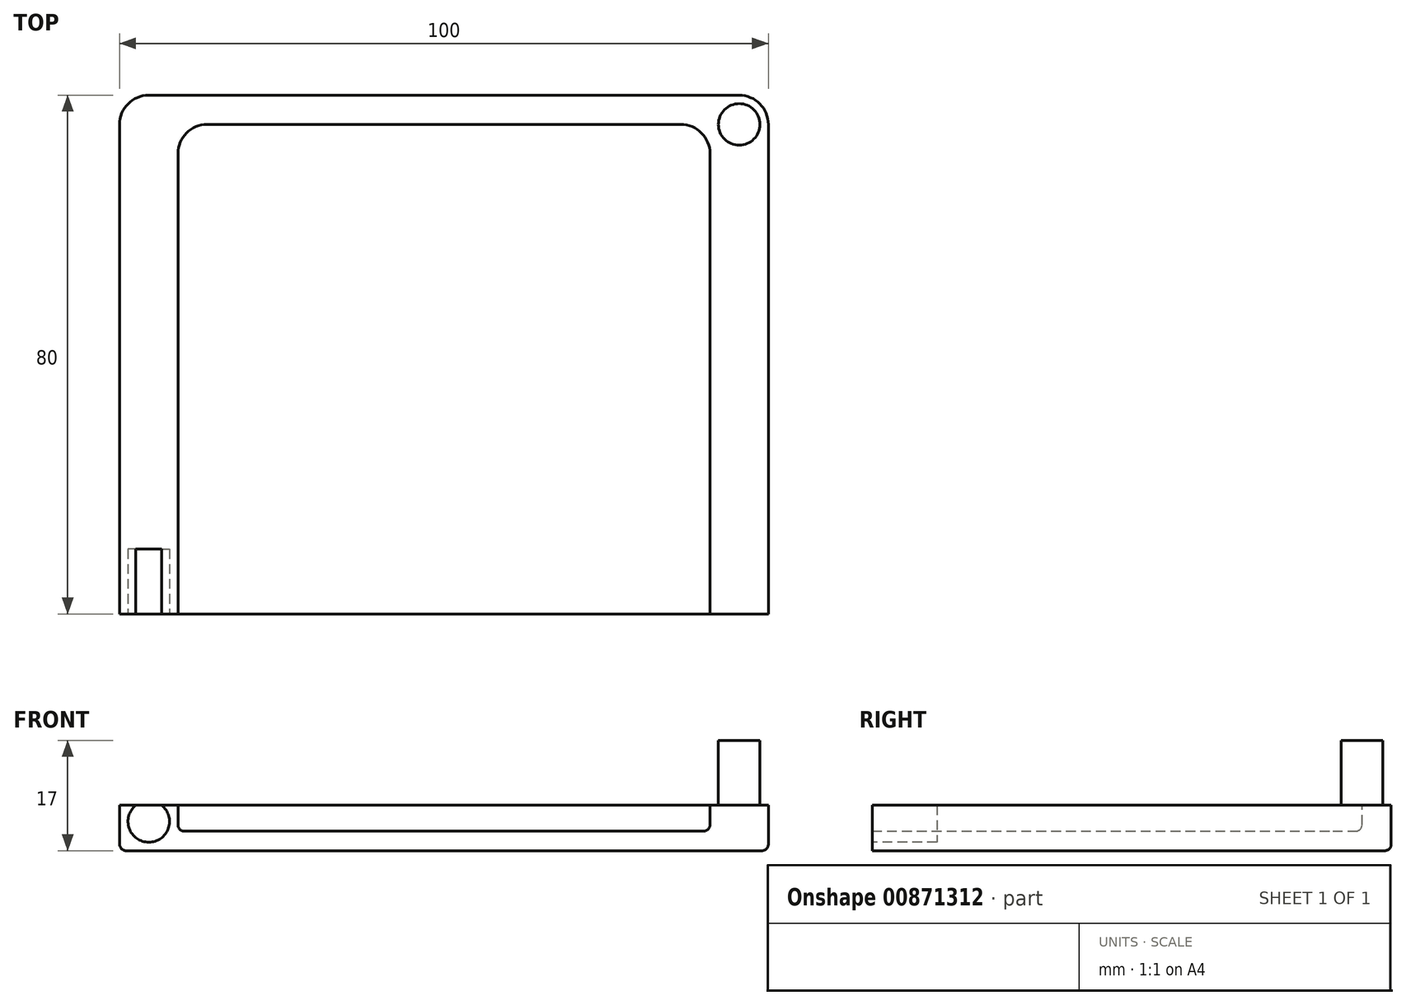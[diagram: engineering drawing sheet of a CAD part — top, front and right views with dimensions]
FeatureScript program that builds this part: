
annotation { "Feature Type Name" : "Feature", "Feature Type Description" : "" }
export const myFeature = defineFeature(function(context is Context, id is Id, definition is map)
    precondition{}
    {
        {
            var Q0;
            Q0=qCreatedBy(makeId("Top.planeOp"),FACE);
            var sketch = newSketch(context, id + "F0", { "sketchPlane" : qUnion([Q0])});
            skLineSegment(sketch, "E0.bottom", {"start": v(0, 0) * mm, "end": v(50, 0) * mm});
            skLineSegment(sketch, "E0.top", {"start": v(4.5, 80) * mm, "end": v(50, 80) * mm});
            skLineSegment(sketch, "E0.left", {"start": v(0, 0) * mm, "end": v(0, 75.5) * mm});
            skLineSegment(sketch, "E0.right", {"start": v(50, 0) * mm, "end": v(50, 80) * mm, "construction": true});
            skPoint(sketch, "E1.visualSharp", {"position": v(0, 80) * mm});
            skArc(sketch, "E1.filletArc", {"start": v(4.5, 80) * mm, "mid": v(1.32, 78.68) * mm, "end": v(0, 75.5) * mm});
            skArc(sketch, "E2.MirrorCS", {"start": v(95.5, 80) * mm, "mid": v(98.68, 78.68) * mm, "end": v(100, 75.5) * mm});
            skLineSegment(sketch, "E3.MirrorCS", {"start": v(100, 0) * mm, "end": v(50, 0) * mm});
            skPoint(sketch, "E4.MirrorP", {"position": v(100, 80) * mm});
            skLineSegment(sketch, "E5.MirrorCS", {"start": v(95.5, 80) * mm, "end": v(50, 80) * mm});
            skLineSegment(sketch, "E6.MirrorCS", {"start": v(100, 0) * mm, "end": v(100, 75.5) * mm});
            skSolve(sketch);
        }
        {
            var Q0;
            Q0=makeQuery(id+"F0.imprint","IMPRINT",FACE,{"disambiguationData":[TD([[makeQuery(id+"F0.imprint","IMPRINT",EDGE,{"derivedFrom":sQuery(id+"F0.wireOp",EDGE,"E0.bottom")}),1.0]])]});
            extrude(context, id + "F1", {"entities" : qUnion([Q0]), "depth" : 17 * mm, "offsetDistance" : 25 * mm});
        }
        {
            var Q0;
            Q0=qCreatedBy(makeId("Top.planeOp"),FACE);
            cPlane(context, id + "F2", {"entities" : qUnion([Q0]), "cplaneType" : CPlaneType.OFFSET, "offset" : 17 * mm, "width" : 150 * mm, "height" : 150 * mm});
        }
        {
            var Q0;
            Q0=qCreatedBy(id+"F2.planeOp",FACE);
            var sketch = newSketch(context, id + "F3", { "sketchPlane" : qUnion([Q0])});
            skLineSegment(sketch, "E7.bottom", {"start": v(0, 0) * mm, "end": v(50, 0) * mm});
            skLineSegment(sketch, "E7.top", {"start": v(4.5, 80) * mm, "end": v(50, 80) * mm});
            skLineSegment(sketch, "E7.left", {"start": v(0, 0) * mm, "end": v(0, 75.5) * mm});
            skLineSegment(sketch, "E7.right", {"start": v(50, 0) * mm, "end": v(50, 80) * mm, "construction": true});
            skPoint(sketch, "E8.visualSharp", {"position": v(0, 80) * mm});
            skArc(sketch, "E8.filletArc", {"start": v(4.5, 80) * mm, "mid": v(1.32, 78.68) * mm, "end": v(0, 75.5) * mm});
            skCircle(sketch, "E9", {"center": v(4.5, 75.5) * mm, "radius": 3.2 * mm});
            skLineSegment(sketch, "E10", {"start": v(9, 0) * mm, "end": v(9, 71) * mm});
            skLineSegment(sketch, "E11", {"start": v(13.5, 75.5) * mm, "end": v(50, 75.5) * mm});
            skPoint(sketch, "E12.visualSharp", {"position": v(9, 75.5) * mm});
            skArc(sketch, "E12.filletArc", {"start": v(13.5, 75.5) * mm, "mid": v(10.32, 74.18) * mm, "end": v(9, 71) * mm});
            skArc(sketch, "E13.MirrorCS", {"start": v(86.5, 75.5) * mm, "mid": v(89.68, 74.18) * mm, "end": v(91, 71) * mm});
            skArc(sketch, "E14.MirrorCS", {"start": v(95.5, 80) * mm, "mid": v(98.68, 78.68) * mm, "end": v(100, 75.5) * mm});
            skPoint(sketch, "E15.MirrorP", {"position": v(91, 75.5) * mm});
            skLineSegment(sketch, "E16.MirrorCS", {"start": v(91, 0) * mm, "end": v(91, 71) * mm});
            skLineSegment(sketch, "E17.MirrorCS", {"start": v(86.5, 75.5) * mm, "end": v(50, 75.5) * mm});
            skCircle(sketch, "E18.MirrorC", {"center": v(95.5, 75.5) * mm, "radius": 3.2 * mm});
            skLineSegment(sketch, "E19.MirrorCS", {"start": v(100, 0) * mm, "end": v(50, 0) * mm});
            skPoint(sketch, "E20.MirrorP", {"position": v(100, 80) * mm});
            skLineSegment(sketch, "E21.MirrorCS", {"start": v(95.5, 80) * mm, "end": v(50, 80) * mm});
            skLineSegment(sketch, "E22.MirrorCS", {"start": v(100, 0) * mm, "end": v(100, 75.5) * mm});
            skSolve(sketch);
        }
        {
            var Q0;
            Q0=qCreatedBy(makeId("Front.planeOp"),FACE);
            var sketch = newSketch(context, id + "F4", { "sketchPlane" : qUnion([Q0])});
            skLineSegment(sketch, "E23", {"start": v(50, 28.4) * mm, "end": v(50, -10.45) * mm, "construction": true});
            skCircle(sketch, "E24", {"center": v(4.5, 4.5) * mm, "radius": 3.2 * mm});
            skCircle(sketch, "E25.MirrorC", {"center": v(95.5, 4.5) * mm, "radius": 3.2 * mm});
            skSolve(sketch);
        }
        {
            var Q0;
            {var subQ0=sQuery(id+"F3.wireOp",EDGE,"E10");Q0=makeQuery(id+"F3.imprint","IMPRINT",FACE,{"disambiguationData":[TD([[makeQuery(id+"F3.imprint","IMPRINT",EDGE,{"derivedFrom":subQ0}),-1.0]])]});}
            extrude(context, id + "F5", {"entities" : qUnion([Q0]), "operationType" : NewBodyOperationType.REMOVE, "oppositeDirection" : true, "depth" : 14 * mm, "offsetDistance" : 25 * mm});
        }
        {
            var Q0;
            Q0=makeQuery(id+"F3.imprint","IMPRINT",FACE,{"disambiguationData":[TD([[makeQuery(id+"F3.imprint","IMPRINT",EDGE,{"derivedFrom":sQuery(id+"F3.wireOp",EDGE,"E9")}),1.0]])]});
            var Q1;
            Q1=makeQuery(id+"F3.imprint","IMPRINT",FACE,{"disambiguationData":[TD([[makeQuery(id+"F3.imprint","IMPRINT",EDGE,{"derivedFrom":sQuery(id+"F3.wireOp",EDGE,"E18.MirrorC")}),-1.0]])]});
            extrude(context, id + "F6", {"entities" : qUnion([Q0, Q1]), "operationType" : NewBodyOperationType.REMOVE, "oppositeDirection" : true, "depth" : 10 * mm, "offsetDistance" : 25 * mm});
        }
        {
            var Q0;
            Q0=makeQuery(id+"F4.imprint","IMPRINT",FACE,{"disambiguationData":[TD([[makeQuery(id+"F4.imprint","IMPRINT",EDGE,{"derivedFrom":sQuery(id+"F4.wireOp",EDGE,"E24")}),1.0]])]});
            var Q1;
            Q1=makeQuery(id+"F4.imprint","IMPRINT",FACE,{"disambiguationData":[TD([[makeQuery(id+"F4.imprint","IMPRINT",EDGE,{"derivedFrom":sQuery(id+"F4.wireOp",EDGE,"E25.MirrorC")}),-1.0]])]});
            extrude(context, id + "F7", {"entities" : qUnion([Q0, Q1]), "operationType" : NewBodyOperationType.REMOVE, "oppositeDirection" : true, "depth" : 10 * mm, "offsetDistance" : 25 * mm});
        }
        {
            var Q0;
            Q0=makeQuery(id+"F5.boolean.opBoolean","COPY",EDGE,{"derivedFrom":makeQuery(id+"F5.opExtrude","CAP_EDGE",EDGE,{"disambiguationData":[OSD([sQuery(id+"F3.wireOp",EDGE,"E11"),sQuery(id+"F3.wireOp",EDGE,"E17.MirrorCS")])],"isStart":false})});
            var Q1;
            Q1=makeQuery(id+"F1.opExtrude","CAP_EDGE",EDGE,{"disambiguationData":[OSD([sQuery(id+"F0.wireOp",EDGE,"E6.MirrorCS")])],"isStart":false});
            var Q2;
            Q2=makeQuery(id+"F1.opExtrude","CAP_EDGE",EDGE,{"disambiguationData":[OSD([sQuery(id+"F0.wireOp",EDGE,"E6.MirrorCS")])],"isStart":true});
            var Q3;
            Q3=makeQuery(id+"F7.boolean.opBoolean","COPY",EDGE,{"derivedFrom":makeQuery(id+"F7.opExtrude","CAP_EDGE",EDGE,{"disambiguationData":[OSD([sQuery(id+"F4.wireOp",EDGE,"E24")])],"isStart":true})});
            var Q4;
            Q4=makeQuery(id+"F7.boolean.opBoolean","COPY",EDGE,{"derivedFrom":makeQuery(id+"F7.opExtrude","CAP_EDGE",EDGE,{"disambiguationData":[OSD([sQuery(id+"F4.wireOp",EDGE,"E25.MirrorC")])],"isStart":true})});
            var Q5;
            Q5=makeQuery(id+"F6.boolean.opBoolean","COPY",EDGE,{"derivedFrom":makeQuery(id+"F6.opExtrude","CAP_EDGE",EDGE,{"disambiguationData":[OSD([sQuery(id+"F3.wireOp",EDGE,"E18.MirrorC")])],"isStart":true})});
            var Q6;
            Q6=makeQuery(id+"F6.boolean.opBoolean","COPY",EDGE,{"derivedFrom":makeQuery(id+"F6.opExtrude","CAP_EDGE",EDGE,{"disambiguationData":[OSD([sQuery(id+"F3.wireOp",EDGE,"E9")])],"isStart":true})});
            var Q7;
            Q7=makeQuery(id+"F5.boolean.opBoolean","COPY",EDGE,{"derivedFrom":makeQuery(id+"F5.opExtrude","CAP_EDGE",EDGE,{"disambiguationData":[OSD([sQuery(id+"F3.wireOp",EDGE,"E10")])],"isStart":true})});
            fillet(context, id + "F8", {"entities" : qUnion([Q0, Q1, Q2, Q3, Q4, Q5, Q6, Q7]), "radius" : 1 * mm, "tangentPropagation" : true, "allowEdgeOverflow" : false});
        }
    });
